# Revit family: Pantalla Modelo ES
name_source: partatom
category: Luminarias
units: mm (PartAtom-declared; Revit-internal decimal feet)

## family parameters
Compartido = No
Corte con vacíos al cargar = No
Cota de conector redondo = Diámetro de uso
Origen de luz = No
Punto de cálculo de habitación = No
Se basa en plano de trabajo = Sí
Siempre vertical = No
Tipo de pieza = Normal

## types (3) — shared parameters
Comentarios de vataje = 100-240V
Espesor = 70 mm  [stored 0.229659 ft]
Fabricante = BRILLANT
Lámpara = SMD
Modulo alto = 600 mm  [stored 1.9685 ft]
Modulo largo = 600 mm  [stored 1.9685 ft]
Watt per fixture = 100
zero-valued in all types: Elevación por defecto

## per-type parameters (varying)
| type | Descripción | Modelo |
| Pantalla Modelo ES_ES6100W.1 | PANTALLA MODELO ES6, PIXEL PITCH 6.25MM, RESOLUCION DE PANEL 96X96 DOTS, CANTIDAD/PANEL 9216 DOTS, CONFIGURACION DE PIXEL SMD 3 EN 1, BRILLO 3000-5000 NITS, ACTUALIZACION 2000Hz, ESCALA DE GRISES 16BITS, AJUSTE DE BRILLO 256 NIVELES, CONTRASTE 1000:1, DIMENSION DEL PANEL 600X600X70MM, PANEL 0.36M2, PESO DEL PANEL 8kg, CONSUMO DE ENERGIA DE 100W, ANGULO DE VISUALIZACION 140/120 GRADOS, TRANSPARENCIA 20%, DISTNACIA DE VISUALIZACION 6M, ANGULO DE ROTACION MAS-MENOS 15 GRADOS, PUNTO DE CONTROL <0.0002, DURACION DE LAS LUCES (50% BRILLO) >50,000 HORAS, TEMPERATURA DE OPERACIÓN 10-90%, HUMEDAD RELATIVA 10-90%, IP 65, VOLTAJE AC 100-240V/50-60Hz, MODO DE ENTRADA CORRIENTE CONSTANTE, SISTEMA OPERATIVO: WINDOWS 2000/XP/VISTA/WINDOWS 7, TIPO DE SEÑAL: AV/S-VIDEO/VGA/CVBS/HDMI/DVI/SDI, CONTROL DE DISTANCIA HSYV <100M. | ES6100W.1 |
| Pantalla Modelo ES_ES9100W.1 | PANTALLA MODELO ES9, PIXEL PITCH 9.3MM, RESOLUCION DE PANEL 64X64 DOTS, CANTIDAD/PANEL 4096 DOTS, CONFIGURACION DE PIXEL SMD 3 EN 1, BRILLO 3000-5000 NITS, ACTUALIZACION 2000Hz, ESCALA DE GRISES 16BITS, AJUSTE DE BRILLO 256 NIVELES, CONTRASTE 1000:1, DIMENSION DEL PANEL 600X600X70MM, PANEL 0.36M2, PESO DEL PANEL 8kg, CONSUMO DE ENERGIA DE 100W, ANGULO DE VISUALIZACION 140/120 GRADOS, TRANSPARENCIA 35%, DISTNACIA DE VISUALIZACION 9M, ANGULO DE ROTACION MAS-MENOS 15 GRADOS, PUNTO DE CONTROL <0.0002, DURACION DE LAS LUCES (50% BRILLO) >50,000 HORAS, TEMPERATURA DE OPERACIÓN 10-90%, HUMEDAD RELATIVA 10-90%, IP 65, VOLTAJE AC 100-240V/50-60Hz, MODO DE ENTRADA CORRIENTE CONSTANTE, SISTEMA OPERATIVO: WINDOWS 2000/XP/VISTA/WINDOWS 7, TIPO DE SEÑAL: AV/S-VIDEO/VGA/CVBS/HDMI/DVI/SDI, CONTROL DE DISTANCIA HSYV <100M. | ES9100W.1 |
| Pantalla Modelo ES_ES12100W.1 | PANTALLA MODELO ES12, PIXEL PITCH 12.5MM, RESOLUCION DE PANEL 48X48 DOTS, CANTIDAD/PANEL 2304 DOTS, CONFIGURACION DE PIXEL SMD 3 EN 1, BRILLO 3000-5000 NITS, ACTUALIZACION 2000Hz, ESCALA DE GRISES 16BITS, AJUSTE DE BRILLO 256 NIVELES, CONTRASTE 1000:1, DIMENSION DEL PANEL 600X600X70MM, PANEL 0.36M2, PESO DEL PANEL 8kg, CONSUMO DE ENERGIA DE 100W, ANGULO DE VISUALIZACION 140/120 GRADOS, TRANSPARENCIA 45%, DISTNACIA DE VISUALIZACION 12M, ANGULO DE ROTACION MAS-MENOS 15 GRADOS, PUNTO DE CONTROL <0.0002, DURACION DE LAS LUCES (50% BRILLO) >50,000 HORAS, TEMPERATURA DE OPERACIÓN 10-90%, HUMEDAD RELATIVA 10-90%, IP 65, VOLTAJE AC 100-240V/50-60Hz, MODO DE ENTRADA CORRIENTE CONSTANTE, SISTEMA OPERATIVO: WINDOWS 2000/XP/VISTA/WINDOWS 7, TIPO DE SEÑAL: AV/S-VIDEO/VGA/CVBS/HDMI/DVI/SDI, CONTROL DE DISTANCIA HSYV <100M. | ES12100W.1 |

note: [stored X ft] marks values corroborated as IEEE doubles in the binary element streams (Revit-internal decimal feet)

## geometry (parser evidence)
native form markers: Blend x2
no freeform markers — native parametric forms only
